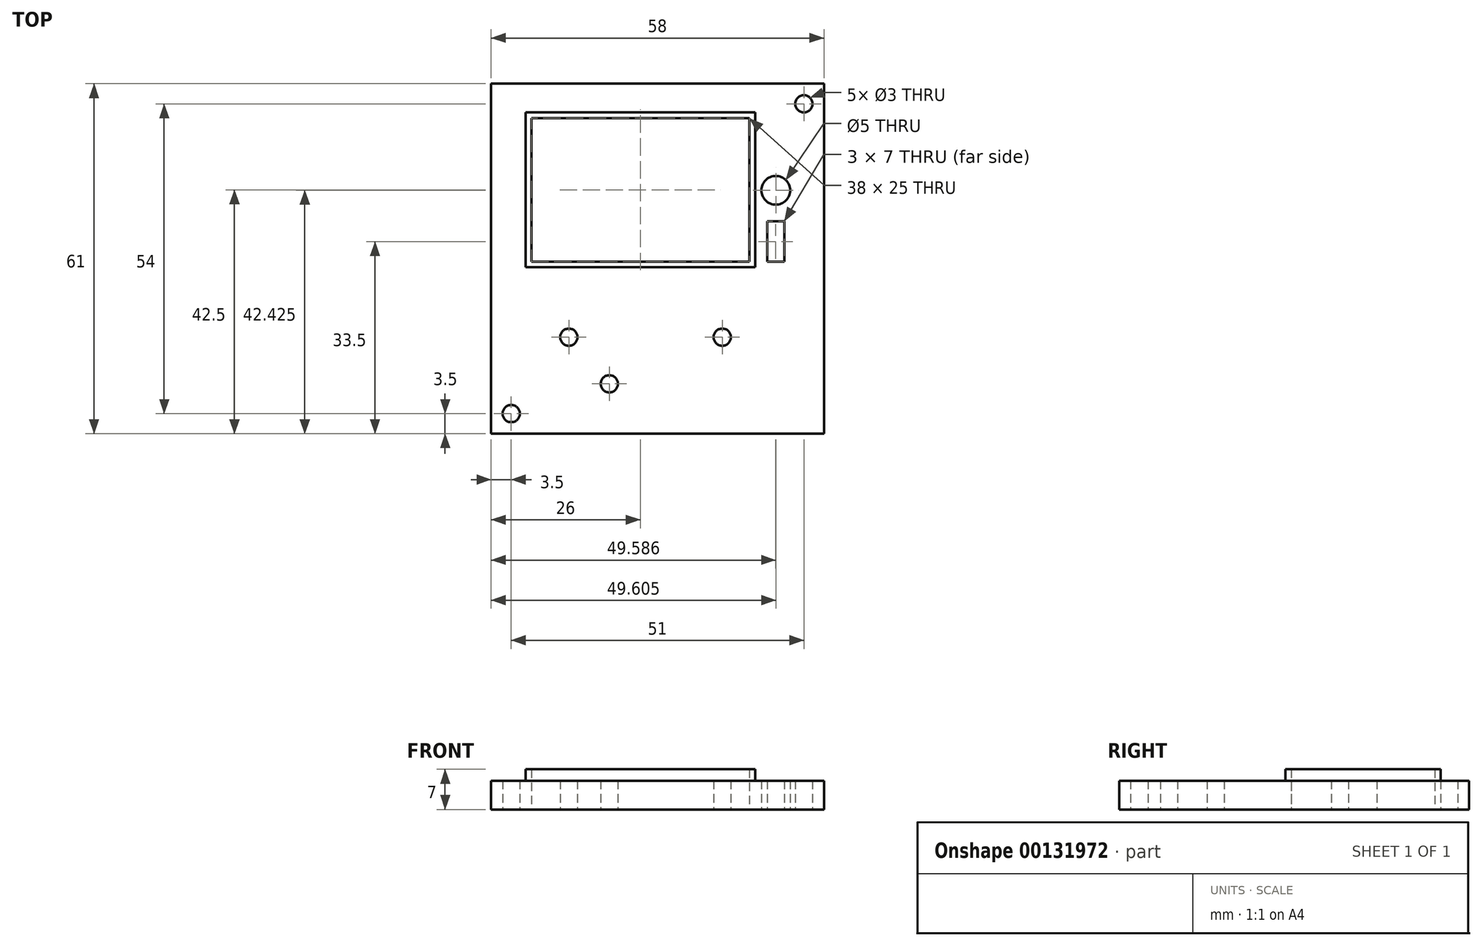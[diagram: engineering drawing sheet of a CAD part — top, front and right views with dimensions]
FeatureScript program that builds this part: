
annotation { "Feature Type Name" : "Feature", "Feature Type Description" : "" }
export const myFeature = defineFeature(function(context is Context, id is Id, definition is map)
    precondition{}
    {
        {
            var Q0;
            Q0=qCreatedBy(makeId("Top.planeOp"),FACE);
            var sketch = newSketch(context, id + "F0", { "sketchPlane" : qUnion([Q0])});
            skLineSegment(sketch, "E0.bottom", {"start": v(0, 0) * mm, "end": v(58, 0) * mm});
            skLineSegment(sketch, "E0.top", {"start": v(0, -61) * mm, "end": v(58, -61) * mm});
            skLineSegment(sketch, "E0.left", {"start": v(0, 0) * mm, "end": v(0, -61) * mm});
            skLineSegment(sketch, "E0.right", {"start": v(58, 0) * mm, "end": v(58, -61) * mm});
            skLineSegment(sketch, "E1.bottom", {"start": v(7, -6) * mm, "end": v(45, -6) * mm});
            skLineSegment(sketch, "E1.top", {"start": v(7, -31) * mm, "end": v(45, -31) * mm});
            skLineSegment(sketch, "E1.left", {"start": v(7, -6) * mm, "end": v(7, -31) * mm});
            skLineSegment(sketch, "E1.right", {"start": v(45, -6) * mm, "end": v(45, -31) * mm});
            skCircle(sketch, "E2", {"center": v(13.54, -44.17) * mm, "radius": 4 * mm, "construction": true});
            skCircle(sketch, "E3", {"center": v(3.5, -57.5) * mm, "radius": 1.5 * mm});
            skCircle(sketch, "E4", {"center": v(40.28, -44.17) * mm, "radius": 6 * mm, "construction": true});
            skLineSegment(sketch, "E5.bottom", {"start": v(48.09, -24) * mm, "end": v(51.09, -24) * mm});
            skLineSegment(sketch, "E5.top", {"start": v(48.09, -31) * mm, "end": v(51.09, -31) * mm});
            skLineSegment(sketch, "E5.left", {"start": v(48.09, -24) * mm, "end": v(48.09, -31) * mm});
            skLineSegment(sketch, "E5.right", {"start": v(51.09, -24) * mm, "end": v(51.09, -31) * mm});
            skCircle(sketch, "E6", {"center": v(54.5, -3.5) * mm, "radius": 1.5 * mm});
            skCircle(sketch, "E7", {"center": v(20.6, -52.3) * mm, "radius": 1.5 * mm});
            skCircle(sketch, "E8", {"center": v(49.6, -18.57) * mm, "radius": 2.5 * mm});
            skCircle(sketch, "E9", {"center": v(13.54, -44.17) * mm, "radius": 1.5 * mm});
            skCircle(sketch, "E10", {"center": v(40.28, -44.17) * mm, "radius": 1.5 * mm});
            skSolve(sketch);
        }
        {
            var Q0;
            Q0=makeQuery(id+"F0.imprint","IMPRINT",FACE,{"disambiguationData":[TD([[makeQuery(id+"F0.imprint","IMPRINT",EDGE,{"derivedFrom":sQuery(id+"F0.wireOp",EDGE,"E0.bottom")}),-1.0]])]});
            extrude(context, id + "F1", {"entities" : qUnion([Q0]), "depth" : 5 * mm});
        }
        {
            var Q0;
            Q0=makeQuery(id+"F1.opExtrude","CAP_FACE",FACE,{"disambiguationData":[OSD([sQuery(id+"F0.wireOp",EDGE,"E0.bottom"),sQuery(id+"F0.wireOp",EDGE,"E0.top"),sQuery(id+"F0.wireOp",EDGE,"E0.left"),sQuery(id+"F0.wireOp",EDGE,"E0.right"),sQuery(id+"F0.wireOp",EDGE,"E1.bottom"),sQuery(id+"F0.wireOp",EDGE,"E1.top"),sQuery(id+"F0.wireOp",EDGE,"E1.left"),sQuery(id+"F0.wireOp",EDGE,"E1.right"),sQuery(id+"F0.wireOp",EDGE,"E3"),sQuery(id+"F0.wireOp",EDGE,"E5.bottom"),sQuery(id+"F0.wireOp",EDGE,"E5.top"),sQuery(id+"F0.wireOp",EDGE,"E5.left"),sQuery(id+"F0.wireOp",EDGE,"E5.right"),sQuery(id+"F0.wireOp",EDGE,"E6"),sQuery(id+"F0.wireOp",EDGE,"E7"),sQuery(id+"F0.wireOp",EDGE,"E8"),sQuery(id+"F0.wireOp",EDGE,"E9"),sQuery(id+"F0.wireOp",EDGE,"E10")])],"isStart":false});
            var sketch = newSketch(context, id + "F2", { "sketchPlane" : qUnion([Q0])});
            skLineSegment(sketch, "E11.bottom", {"start": v(7, -6) * mm, "end": v(45, -6) * mm});
            skLineSegment(sketch, "E11.top", {"start": v(7, -31) * mm, "end": v(45, -31) * mm});
            skLineSegment(sketch, "E11.left", {"start": v(7, -6) * mm, "end": v(7, -31) * mm});
            skLineSegment(sketch, "E11.right", {"start": v(45, -6) * mm, "end": v(45, -31) * mm});
            skLineSegment(sketch, "E12.bottom", {"start": v(6, -5) * mm, "end": v(46, -5) * mm});
            skLineSegment(sketch, "E12.top", {"start": v(6, -32) * mm, "end": v(46, -32) * mm});
            skLineSegment(sketch, "E12.left", {"start": v(6, -5) * mm, "end": v(6, -32) * mm});
            skLineSegment(sketch, "E12.right", {"start": v(46, -5) * mm, "end": v(46, -32) * mm});
            skSolve(sketch);
        }
        {
            var Q0;
            Q0 = qSketchRegion(id + "F2", true);
            extrude(context, id + "F3", {"entities" : qUnion([Q0]), "operationType" : NewBodyOperationType.ADD, "depth" : 2 * mm});
        }
    });
